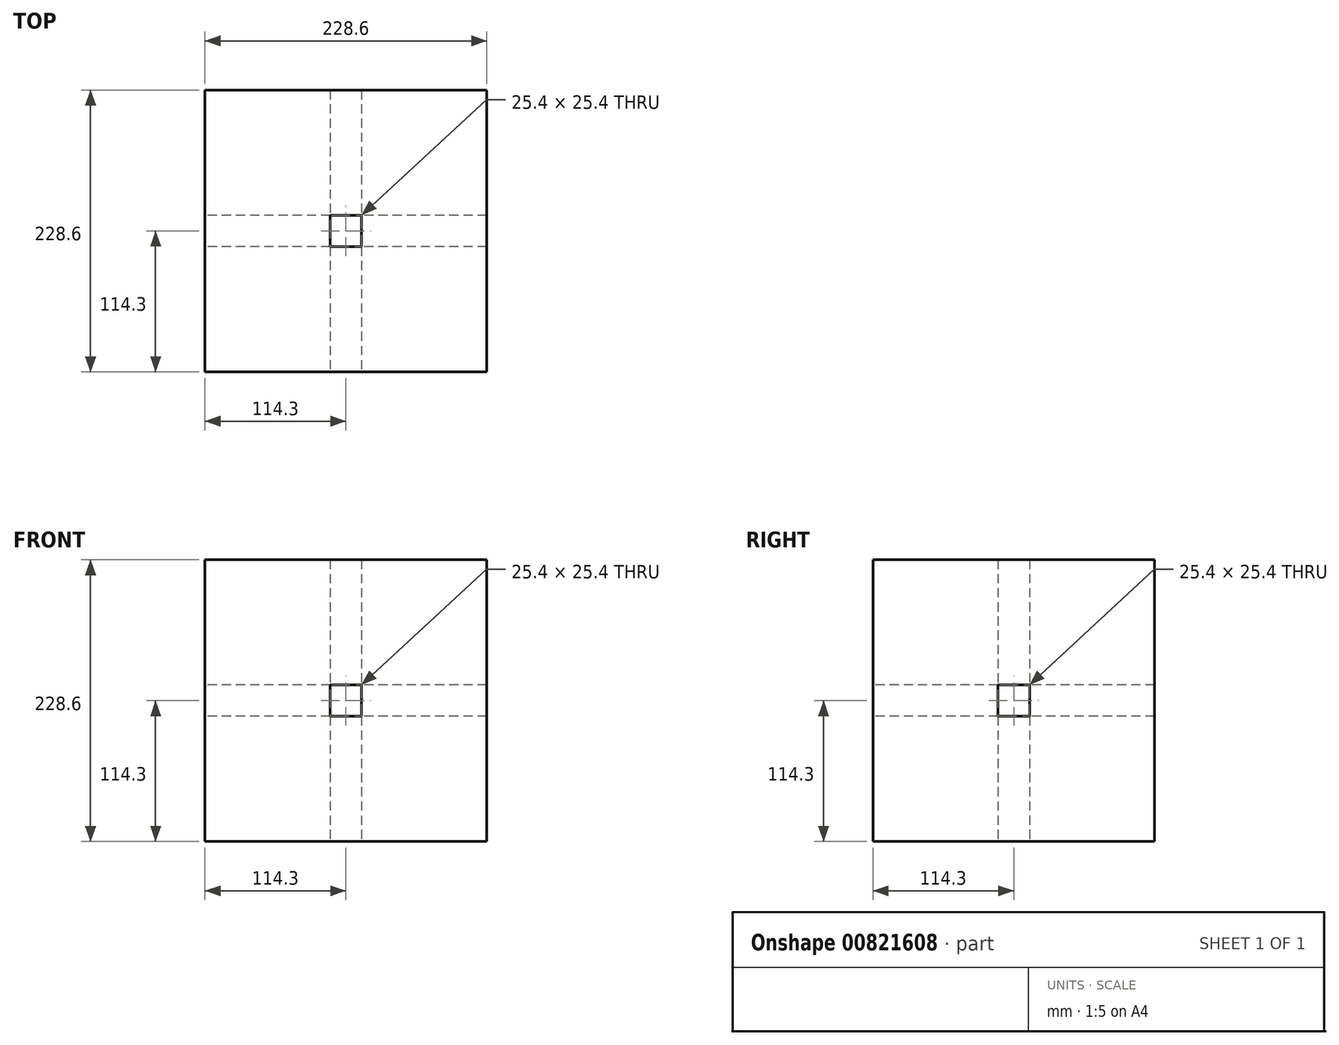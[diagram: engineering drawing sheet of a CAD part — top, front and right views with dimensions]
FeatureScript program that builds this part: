
annotation { "Feature Type Name" : "Feature", "Feature Type Description" : "" }
export const myFeature = defineFeature(function(context is Context, id is Id, definition is map)
    precondition{}
    {
        {
            var Q0;
            Q0=qCreatedBy(makeId("Top.planeOp"),FACE);
            var sketch = newSketch(context, id + "F0", { "sketchPlane" : qUnion([Q0])});
            skLineSegment(sketch, "E0.bottom", {"start": v(114.3, 114.3) * mm, "end": v(-114.3, 114.3) * mm});
            skLineSegment(sketch, "E0.top", {"start": v(114.3, -114.3) * mm, "end": v(-114.3, -114.3) * mm});
            skLineSegment(sketch, "E0.left", {"start": v(114.3, 114.3) * mm, "end": v(114.3, -114.3) * mm});
            skLineSegment(sketch, "E0.right", {"start": v(-114.3, 114.3) * mm, "end": v(-114.3, -114.3) * mm});
            skPoint(sketch, "E0.middle", {"position": v(0, 0) * mm});
            skLineSegment(sketch, "E1.bottom", {"start": v(12.7, 12.7) * mm, "end": v(-12.7, 12.7) * mm});
            skLineSegment(sketch, "E1.top", {"start": v(12.7, -12.7) * mm, "end": v(-12.7, -12.7) * mm});
            skLineSegment(sketch, "E1.left", {"start": v(12.7, 12.7) * mm, "end": v(12.7, -12.7) * mm});
            skLineSegment(sketch, "E1.right", {"start": v(-12.7, 12.7) * mm, "end": v(-12.7, -12.7) * mm});
            skSolve(sketch);
        }
        {
            var Q0;
            Q0=makeQuery(id+"F0.imprint","IMPRINT",FACE,{"disambiguationData":[TD([[makeQuery(id+"F0.imprint","IMPRINT",EDGE,{"derivedFrom":sQuery(id+"F0.wireOp",EDGE,"E0.bottom")}),1.0]])]});
            extrude(context, id + "F1", {"entities" : qUnion([Q0]), "depth" : 114.3 * mm, "offsetDistance" : 25.4 * mm});
        }
        {
            var Q0;
            Q0=makeQuery(id+"F0.imprint","IMPRINT",FACE,{"disambiguationData":[TD([[makeQuery(id+"F0.imprint","IMPRINT",EDGE,{"derivedFrom":sQuery(id+"F0.wireOp",EDGE,"E0.bottom")}),1.0]])]});
            extrude(context, id + "F2", {"entities" : qUnion([Q0]), "operationType" : NewBodyOperationType.ADD, "oppositeDirection" : true, "depth" : 114.3 * mm, "offsetDistance" : 25.4 * mm});
        }
        {
            var Q0;
            {var subQ0=sQuery(id+"F0.wireOp",EDGE,"E0.top");Q0=makeQuery(id+"F2.boolean.opBoolean","MERGE",FACE,{"derivedFrom":[makeQuery(id+"F1.opExtrude","SWEPT_FACE",FACE,{"disambiguationData":[OSD([subQ0])]}),makeQuery(id+"F2.opExtrude","SWEPT_FACE",FACE,{"disambiguationData":[OSD([subQ0])]})]});}
            var sketch = newSketch(context, id + "F3", { "sketchPlane" : qUnion([Q0])});
            skLineSegment(sketch, "E2.bottom", {"start": v(12.7, 12.7) * mm, "end": v(-12.7, 12.7) * mm});
            skLineSegment(sketch, "E2.top", {"start": v(12.7, -12.7) * mm, "end": v(-12.7, -12.7) * mm});
            skLineSegment(sketch, "E2.left", {"start": v(12.7, 12.7) * mm, "end": v(12.7, -12.7) * mm});
            skLineSegment(sketch, "E2.right", {"start": v(-12.7, 12.7) * mm, "end": v(-12.7, -12.7) * mm});
            skPoint(sketch, "E2.middle", {"position": v(0, 0) * mm});
            skSolve(sketch);
        }
        {
            var Q0;
            Q0=makeQuery(id+"F3.imprint","IMPRINT",FACE,{"disambiguationData":[TD([[makeQuery(id+"F3.imprint","IMPRINT",EDGE,{"derivedFrom":sQuery(id+"F3.wireOp",EDGE,"E2.bottom")}),1.0]])]});
            extrude(context, id + "F4", {"entities" : qUnion([Q0]), "operationType" : NewBodyOperationType.REMOVE, "oppositeDirection" : true, "depth" : 228.6 * mm, "offsetDistance" : 25.4 * mm});
        }
        {
            var Q0;
            {var subQ0=sQuery(id+"F0.wireOp",EDGE,"E0.right");Q0=makeQuery(id+"F2.boolean.opBoolean","MERGE",FACE,{"derivedFrom":[makeQuery(id+"F1.opExtrude","SWEPT_FACE",FACE,{"disambiguationData":[OSD([subQ0])]}),makeQuery(id+"F2.opExtrude","SWEPT_FACE",FACE,{"disambiguationData":[OSD([subQ0])]})]});}
            var sketch = newSketch(context, id + "F5", { "sketchPlane" : qUnion([Q0])});
            skLineSegment(sketch, "E3.bottom", {"start": v(12.7, 12.7) * mm, "end": v(-12.7, 12.7) * mm});
            skLineSegment(sketch, "E3.top", {"start": v(12.7, -12.7) * mm, "end": v(-12.7, -12.7) * mm});
            skLineSegment(sketch, "E3.left", {"start": v(12.7, 12.7) * mm, "end": v(12.7, -12.7) * mm});
            skLineSegment(sketch, "E3.right", {"start": v(-12.7, 12.7) * mm, "end": v(-12.7, -12.7) * mm});
            skPoint(sketch, "E3.middle", {"position": v(0, 0) * mm});
            skSolve(sketch);
        }
        {
            var Q0;
            Q0=makeQuery(id+"F5.imprint","IMPRINT",FACE,{"disambiguationData":[TD([[makeQuery(id+"F5.imprint","IMPRINT",EDGE,{"derivedFrom":sQuery(id+"F5.wireOp",EDGE,"E3.bottom")}),1.0]])]});
            extrude(context, id + "F6", {"entities" : qUnion([Q0]), "operationType" : NewBodyOperationType.REMOVE, "oppositeDirection" : true, "depth" : 228.6 * mm, "offsetDistance" : 25.4 * mm});
        }
    });
